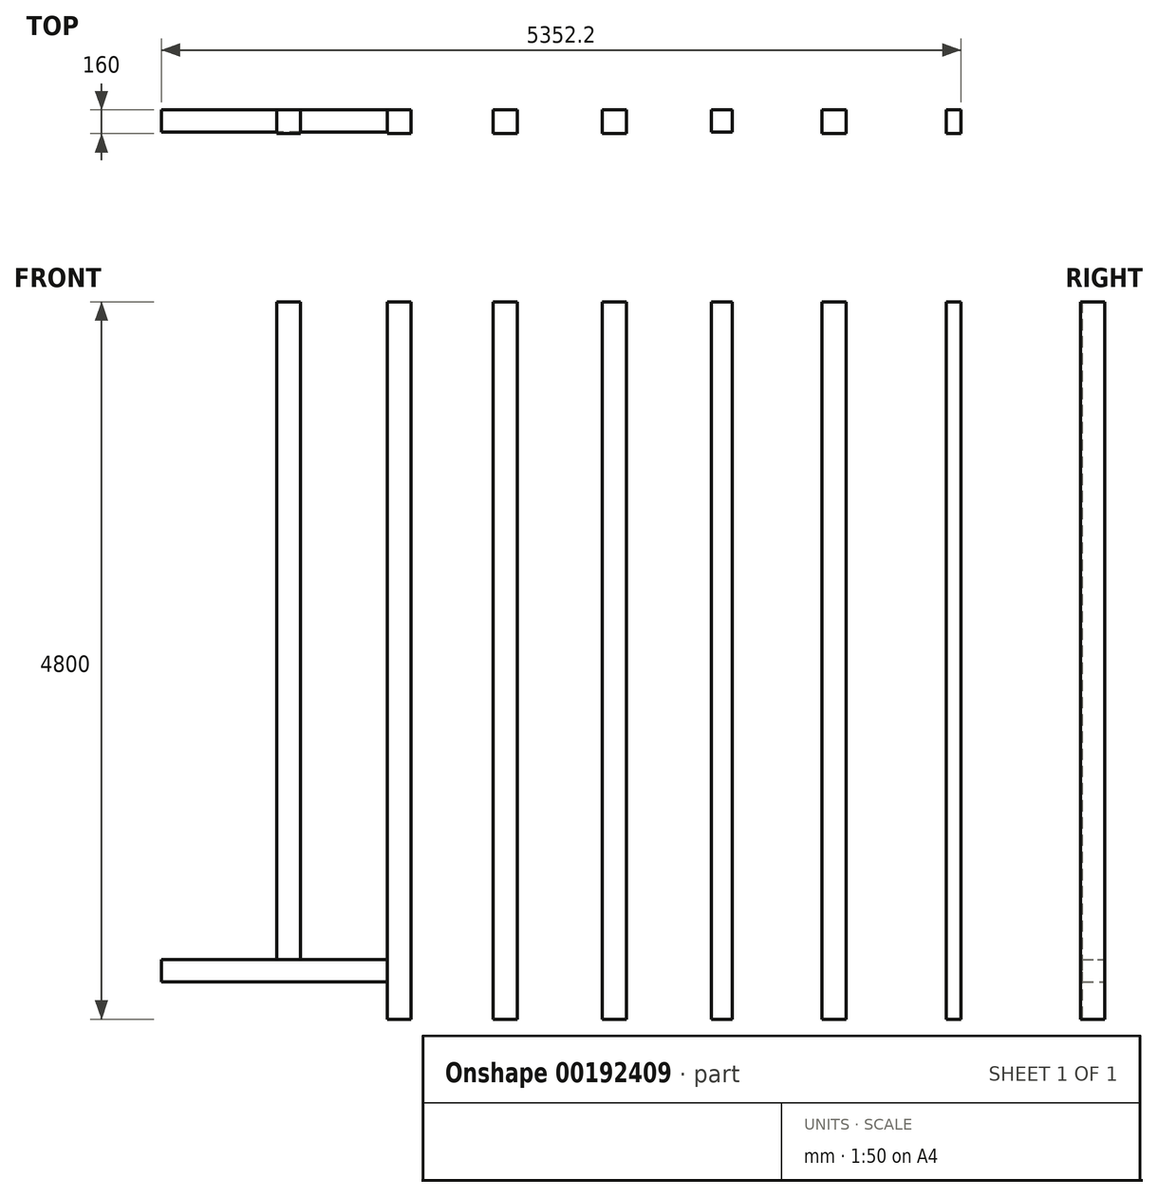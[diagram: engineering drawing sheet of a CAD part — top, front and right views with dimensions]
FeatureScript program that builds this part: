
annotation { "Feature Type Name" : "Feature", "Feature Type Description" : "" }
export const myFeature = defineFeature(function(context is Context, id is Id, definition is map)
    precondition{}
    {
        {
            var Q0;
            Q0=qCreatedBy(makeId("Front.planeOp"),FACE);
            var sketch = newSketch(context, id + "F0", { "sketchPlane" : qUnion([Q0])});
            skLineSegment(sketch, "E0.bottom", {"start": v(80, 2400) * mm, "end": v(-80, 2400) * mm});
            skLineSegment(sketch, "E0.top", {"start": v(80, -2400) * mm, "end": v(-80, -2400) * mm});
            skLineSegment(sketch, "E0.left", {"start": v(80, 2400) * mm, "end": v(80, -2400) * mm});
            skLineSegment(sketch, "E0.right", {"start": v(-80, 2400) * mm, "end": v(-80, -2400) * mm});
            skPoint(sketch, "E0.middle", {"position": v(0, 0) * mm});
            skLineSegment(sketch, "E1.bottom", {"start": v(790, 2400) * mm, "end": v(650, 2400) * mm});
            skLineSegment(sketch, "E1.top", {"start": v(790, -2400) * mm, "end": v(650, -2400) * mm});
            skLineSegment(sketch, "E1.left", {"start": v(790, 2400) * mm, "end": v(790, -2400) * mm});
            skLineSegment(sketch, "E1.right", {"start": v(650, 2400) * mm, "end": v(650, -2400) * mm});
            skLineSegment(sketch, "E2.bottom", {"start": v(1390, 2400) * mm, "end": v(1550, 2400) * mm});
            skLineSegment(sketch, "E2.top", {"start": v(1390, -2400) * mm, "end": v(1550, -2400) * mm});
            skLineSegment(sketch, "E2.left", {"start": v(1390, 2400) * mm, "end": v(1390, -2400) * mm});
            skLineSegment(sketch, "E2.right", {"start": v(1550, 2400) * mm, "end": v(1550, -2400) * mm});
            skLineSegment(sketch, "E3.bottom", {"start": v(2220, 2400) * mm, "end": v(2320, 2400) * mm});
            skLineSegment(sketch, "E3.top", {"start": v(2220, -2400) * mm, "end": v(2320, -2400) * mm});
            skLineSegment(sketch, "E3.left", {"start": v(2220, 2400) * mm, "end": v(2220, -2400) * mm});
            skLineSegment(sketch, "E3.right", {"start": v(2320, 2400) * mm, "end": v(2320, -2400) * mm});
            skLineSegment(sketch, "E4.bottom", {"start": v(-650, 2400) * mm, "end": v(-810, 2400) * mm});
            skLineSegment(sketch, "E4.top", {"start": v(-650, -2400) * mm, "end": v(-810, -2400) * mm});
            skLineSegment(sketch, "E4.left", {"start": v(-650, 2400) * mm, "end": v(-650, -2400) * mm});
            skLineSegment(sketch, "E4.right", {"start": v(-810, 2400) * mm, "end": v(-810, -2400) * mm});
            skLineSegment(sketch, "E5.bottom", {"start": v(-1360, 2400) * mm, "end": v(-1520, 2400) * mm});
            skLineSegment(sketch, "E5.top", {"start": v(-1360, -2400) * mm, "end": v(-1520, -2400) * mm});
            skLineSegment(sketch, "E5.left", {"start": v(-1360, 2400) * mm, "end": v(-1360, -2400) * mm});
            skLineSegment(sketch, "E5.right", {"start": v(-1520, 2400) * mm, "end": v(-1520, -2400) * mm});
            skLineSegment(sketch, "E6.bottom", {"start": v(-2100, 2400) * mm, "end": v(-2260, 2400) * mm});
            skLineSegment(sketch, "E6.left", {"start": v(-2100, 2400) * mm, "end": v(-2100, -2000) * mm});
            skLineSegment(sketch, "E7", {"start": v(-1520, -2000) * mm, "end": v(-2100, -2000) * mm});
            skLineSegment(sketch, "E8", {"start": v(-1520, -2150) * mm, "end": v(-3032.2, -2150) * mm});
            skLineSegment(sketch, "E9", {"start": v(-3032.2, -2150) * mm, "end": v(-3032.2, -2000) * mm});
            skLineSegment(sketch, "E10", {"start": v(-3032.2, -2000) * mm, "end": v(-2260, -2000) * mm});
            skLineSegment(sketch, "E11", {"start": v(-2260, -2000) * mm, "end": v(-2260, 2400) * mm});
            skLineSegment(sketch, "E12", {"start": v(-2260, -2000) * mm, "end": v(-2100, -2000) * mm});
            skSolve(sketch);
        }
        {
            var Q0;
            Q0=makeQuery(id+"F0.imprint","IMPRINT",FACE,{"disambiguationData":[TD([[makeQuery(id+"F0.imprint","IMPRINT",EDGE,{"derivedFrom":sQuery(id+"F0.wireOp",EDGE,"E3.bottom")}),-1.0]])]});
            var Q1;
            Q1=makeQuery(id+"F0.imprint","IMPRINT",FACE,{"disambiguationData":[TD([[makeQuery(id+"F0.imprint","IMPRINT",EDGE,{"derivedFrom":sQuery(id+"F0.wireOp",EDGE,"E2.bottom")}),-1.0]])]});
            var Q2;
            Q2=makeQuery(id+"F0.imprint","IMPRINT",FACE,{"disambiguationData":[TD([[makeQuery(id+"F0.imprint","IMPRINT",EDGE,{"derivedFrom":sQuery(id+"F0.wireOp",EDGE,"E0.bottom")}),1.0]])]});
            var Q3;
            Q3=makeQuery(id+"F0.imprint","IMPRINT",FACE,{"disambiguationData":[TD([[makeQuery(id+"F0.imprint","IMPRINT",EDGE,{"derivedFrom":sQuery(id+"F0.wireOp",EDGE,"E4.bottom")}),1.0]])]});
            var Q4;
            {var subQ1=sQuery(id+"F0.wireOp",EDGE,"E5.bottom");Q4=makeQuery(id+"F0.imprint","IMPRINT",FACE,{"disambiguationData":[TD([[makeQuery(id+"F0.imprint","IMPRINT",EDGE,{"derivedFrom":subQ1}),1.0]])]});}
            var Q5;
            Q5=makeQuery(id+"F0.imprint","IMPRINT",FACE,{"disambiguationData":[TD([[makeQuery(id+"F0.imprint","IMPRINT",EDGE,{"derivedFrom":sQuery(id+"F0.wireOp",EDGE,"E6.bottom")}),1.0]])]});
            extrude(context, id + "F1", {"entities" : qUnion([Q0, Q1, Q2, Q3, Q4, Q5]), "depth" : 160 * mm});
        }
        {
            var Q0;
            {var subQ1=sQuery(id+"F0.wireOp",EDGE,"E7");Q0=makeQuery(id+"F0.imprint","IMPRINT",FACE,{"disambiguationData":[TD([[makeQuery(id+"F0.imprint","IMPRINT",EDGE,{"derivedFrom":subQ1}),1.0]])]});}
            var Q1;
            Q1=makeQuery(id+"F0.imprint","IMPRINT",FACE,{"disambiguationData":[TD([[makeQuery(id+"F0.imprint","IMPRINT",EDGE,{"derivedFrom":sQuery(id+"F0.wireOp",EDGE,"E1.bottom")}),1.0]])]});
            extrude(context, id + "F2", {"entities" : qUnion([Q0, Q1]), "depth" : 150 * mm});
        }
    });
